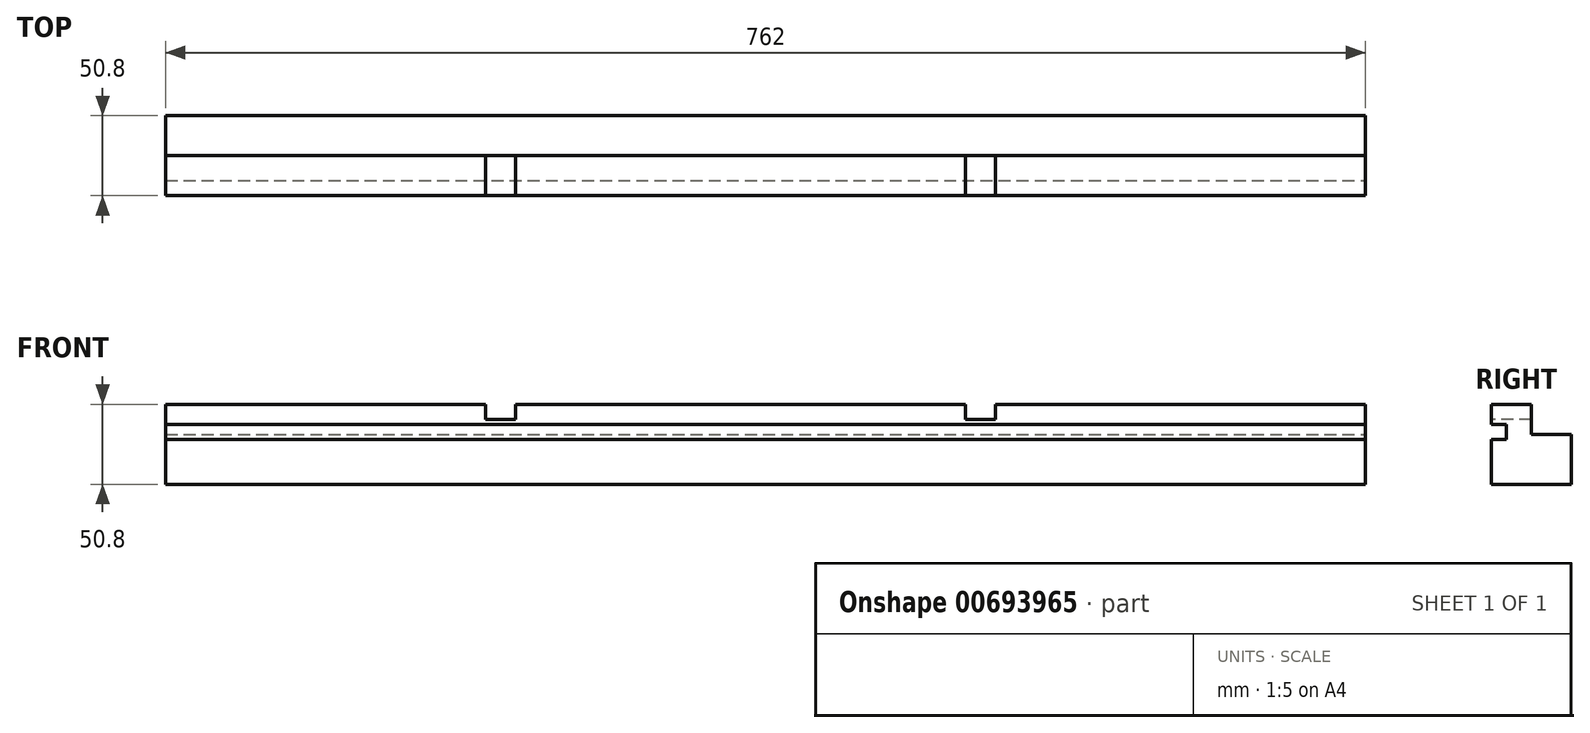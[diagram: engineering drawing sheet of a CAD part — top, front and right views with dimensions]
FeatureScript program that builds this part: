
annotation { "Feature Type Name" : "Feature", "Feature Type Description" : "" }
export const myFeature = defineFeature(function(context is Context, id is Id, definition is map)
    precondition{}
    {
        {
            var Q0;
            Q0=qCreatedBy(makeId("Right.planeOp"),FACE);
            var sketch = newSketch(context, id + "F0", { "sketchPlane" : qUnion([Q0])});
            skLineSegment(sketch, "E0.bottom", {"start": v(0, 0) * mm, "end": v(50.8, 0) * mm});
            skLineSegment(sketch, "E0.top", {"start": v(0, 50.8) * mm, "end": v(50.8, 50.8) * mm});
            skLineSegment(sketch, "E0.left", {"start": v(0, 0) * mm, "end": v(0, 50.8) * mm});
            skLineSegment(sketch, "E0.right", {"start": v(50.8, 0) * mm, "end": v(50.8, 50.8) * mm});
            skLineSegment(sketch, "E1.bottom", {"start": v(0, 38.1) * mm, "end": v(9.52, 38.1) * mm});
            skLineSegment(sketch, "E1.top", {"start": v(0, 28.57) * mm, "end": v(9.52, 28.57) * mm});
            skLineSegment(sketch, "E1.left", {"start": v(0, 38.1) * mm, "end": v(0, 28.57) * mm});
            skLineSegment(sketch, "E1.right", {"start": v(9.52, 38.1) * mm, "end": v(9.52, 28.57) * mm});
            skLineSegment(sketch, "E2.bottom", {"start": v(25.4, 50.8) * mm, "end": v(50.8, 50.8) * mm});
            skLineSegment(sketch, "E2.top", {"start": v(25.4, 31.75) * mm, "end": v(50.8, 31.75) * mm});
            skLineSegment(sketch, "E2.left", {"start": v(25.4, 50.8) * mm, "end": v(25.4, 31.75) * mm});
            skLineSegment(sketch, "E2.right", {"start": v(50.8, 50.8) * mm, "end": v(50.8, 31.75) * mm});
            skSolve(sketch);
        }
        {
            var Q0;
            {var subQ1=sQuery(id+"F0.wireOp",EDGE,"E0.bottom");Q0=makeQuery(id+"F0.imprint","IMPRINT",FACE,{"disambiguationData":[TD([[makeQuery(id+"F0.imprint","IMPRINT",EDGE,{"derivedFrom":subQ1}),1.0]])]});}
            extrude(context, id + "F1", {"entities" : qUnion([Q0]), "oppositeDirection" : true, "depth" : 762 * mm, "offsetDistance" : 25.4 * mm});
        }
        {
            var Q0;
            {var subQ0=sQuery(id+"F0.wireOp",EDGE,"E0.left");Q0=makeQuery(id+"F1.opExtrude","SWEPT_FACE",FACE,{"disambiguationData":[OSD([subQ0]),TDD([makeQuery(id+"F0.imprint","IMPRINT",EDGE,{"disambiguationData":[TD([[makeQuery(id+"F0.imprint","INTERSECT",VERTEX,{"derivedFrom":[sQuery(id+"F0.wireOp",EDGE,"E0.top"),subQ0]}),1.0]])],"derivedFrom":subQ0})])]});}
            var sketch = newSketch(context, id + "F2", { "sketchPlane" : qUnion([Q0])});
            skLineSegment(sketch, "E3.bottom", {"start": v(-558.8, 50.8) * mm, "end": v(-539.75, 50.8) * mm});
            skLineSegment(sketch, "E3.top", {"start": v(-558.8, 41.28) * mm, "end": v(-539.75, 41.28) * mm});
            skLineSegment(sketch, "E3.left", {"start": v(-558.8, 50.8) * mm, "end": v(-558.8, 41.28) * mm});
            skLineSegment(sketch, "E3.right", {"start": v(-539.75, 50.8) * mm, "end": v(-539.75, 41.28) * mm});
            skLineSegment(sketch, "E4.1.0.0", {"start": v(-254, 50.8) * mm, "end": v(-234.95, 50.8) * mm});
            skLineSegment(sketch, "E4.1.0.1", {"start": v(-254, 41.28) * mm, "end": v(-234.95, 41.28) * mm});
            skLineSegment(sketch, "E4.1.0.2", {"start": v(-254, 50.8) * mm, "end": v(-254, 41.28) * mm});
            skLineSegment(sketch, "E4.1.0.3", {"start": v(-234.95, 50.8) * mm, "end": v(-234.95, 41.28) * mm});
            skLineSegment(sketch, "E4.direction1", {"start": v(-558.8, 41.28) * mm, "end": v(-254, 41.28) * mm, "construction": true});
            skSolve(sketch);
        }
        {
            var Q0;
            Q0=makeQuery(id+"F2.imprint","IMPRINT",FACE,{"disambiguationData":[TD([[makeQuery(id+"F2.imprint","IMPRINT",EDGE,{"derivedFrom":sQuery(id+"F2.wireOp",EDGE,"E3.bottom")}),-1.0]])]});
            var Q1;
            Q1=makeQuery(id+"F2.imprint","IMPRINT",FACE,{"disambiguationData":[TD([[makeQuery(id+"F2.imprint","IMPRINT",EDGE,{"derivedFrom":sQuery(id+"F2.wireOp",EDGE,"E4.1.0.0")}),-1.0]])]});
            extrude(context, id + "F3", {"entities" : qUnion([Q0, Q1]), "operationType" : NewBodyOperationType.REMOVE, "oppositeDirection" : true, "depth" : 25.4 * mm, "offsetDistance" : 25.4 * mm});
        }
    });
